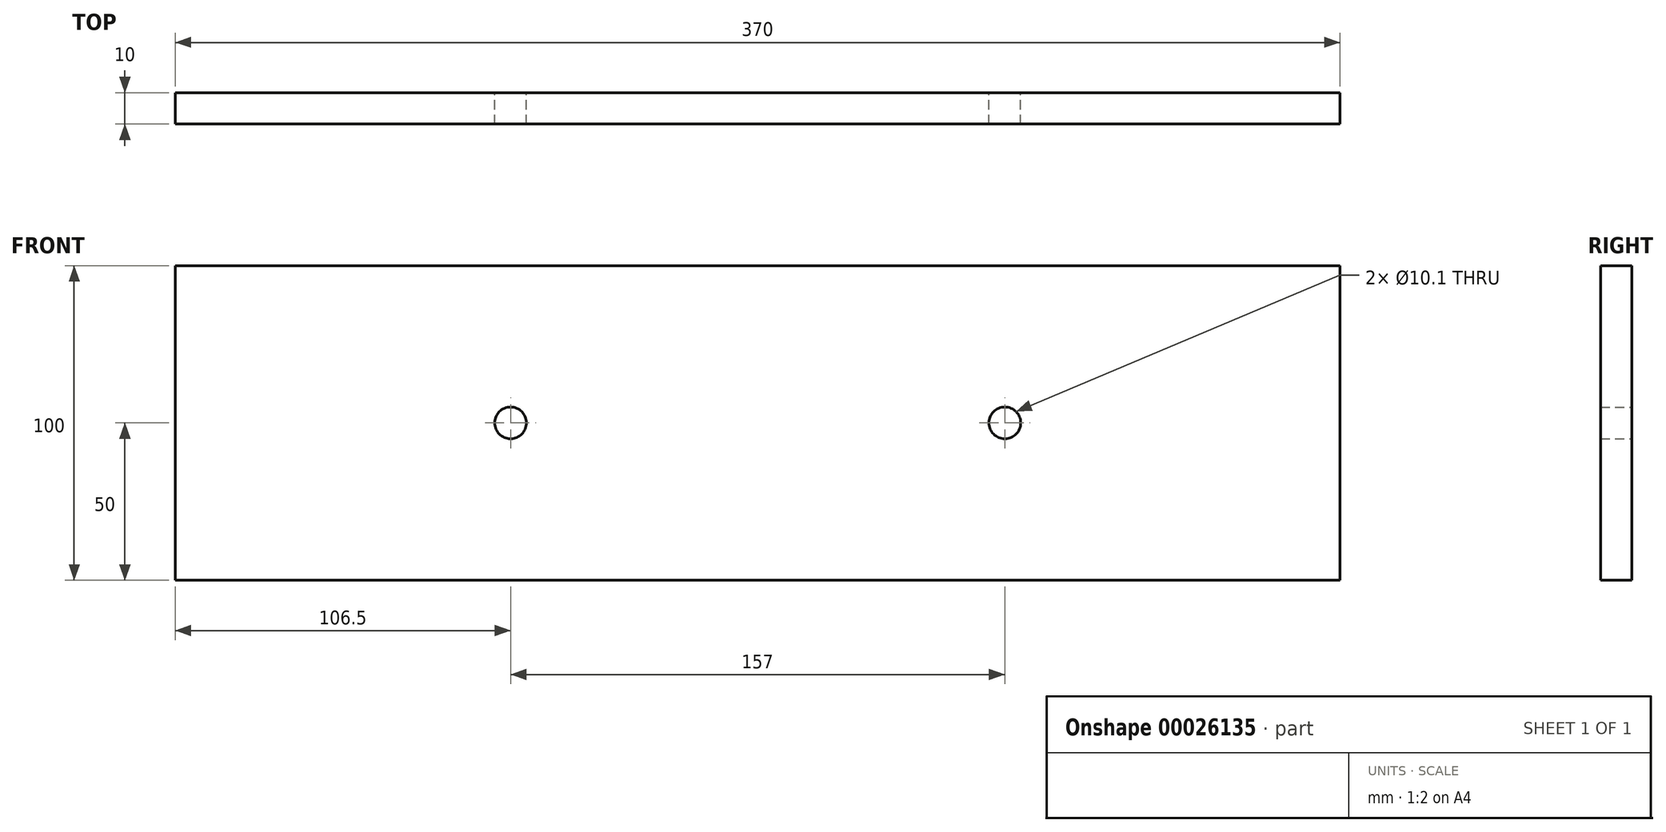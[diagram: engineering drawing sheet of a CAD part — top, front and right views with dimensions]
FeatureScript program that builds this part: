
annotation { "Feature Type Name" : "Feature", "Feature Type Description" : "" }
export const myFeature = defineFeature(function(context is Context, id is Id, definition is map)
    precondition{}
    {
        {
            var Q0;
            Q0=qCreatedBy(makeId("Front.planeOp"),FACE);
            var sketch = newSketch(context, id + "F0", { "sketchPlane" : qUnion([Q0])});
            skLineSegment(sketch, "E0.rect.bottom", {"start": v(185, -50) * mm, "end": v(-185, -50) * mm});
            skLineSegment(sketch, "E0.rect.top", {"start": v(185, 50) * mm, "end": v(-185, 50) * mm});
            skLineSegment(sketch, "E0.rect.left", {"start": v(185, -50) * mm, "end": v(185, 50) * mm});
            skLineSegment(sketch, "E0.rect.right", {"start": v(-185, -50) * mm, "end": v(-185, 50) * mm});
            skPoint(sketch, "E0.rect.middle", {"position": v(0, 0) * mm});
            skLineSegment(sketch, "E1", {"start": v(78.5, 0) * mm, "end": v(-78.5, 0) * mm, "construction": true});
            skCircle(sketch, "E2", {"center": v(-78.5, 0) * mm, "radius": 5.05 * mm});
            skCircle(sketch, "E3", {"center": v(78.5, 0) * mm, "radius": 5.05 * mm});
            skSolve(sketch);
        }
        {
            var Q0;
            Q0=makeQuery(id+"F0.imprint","IMPRINT",FACE,{"disambiguationData":[TD([[makeQuery(id+"F0.imprint","IMPRINT",EDGE,{"derivedFrom":sQuery(id+"F0.wireOp",EDGE,"E0.rect.bottom")}),-1.0]])]});
            extrude(context, id + "F1", {"entities" : qUnion([Q0]), "depth" : 10 * mm});
        }
    });
